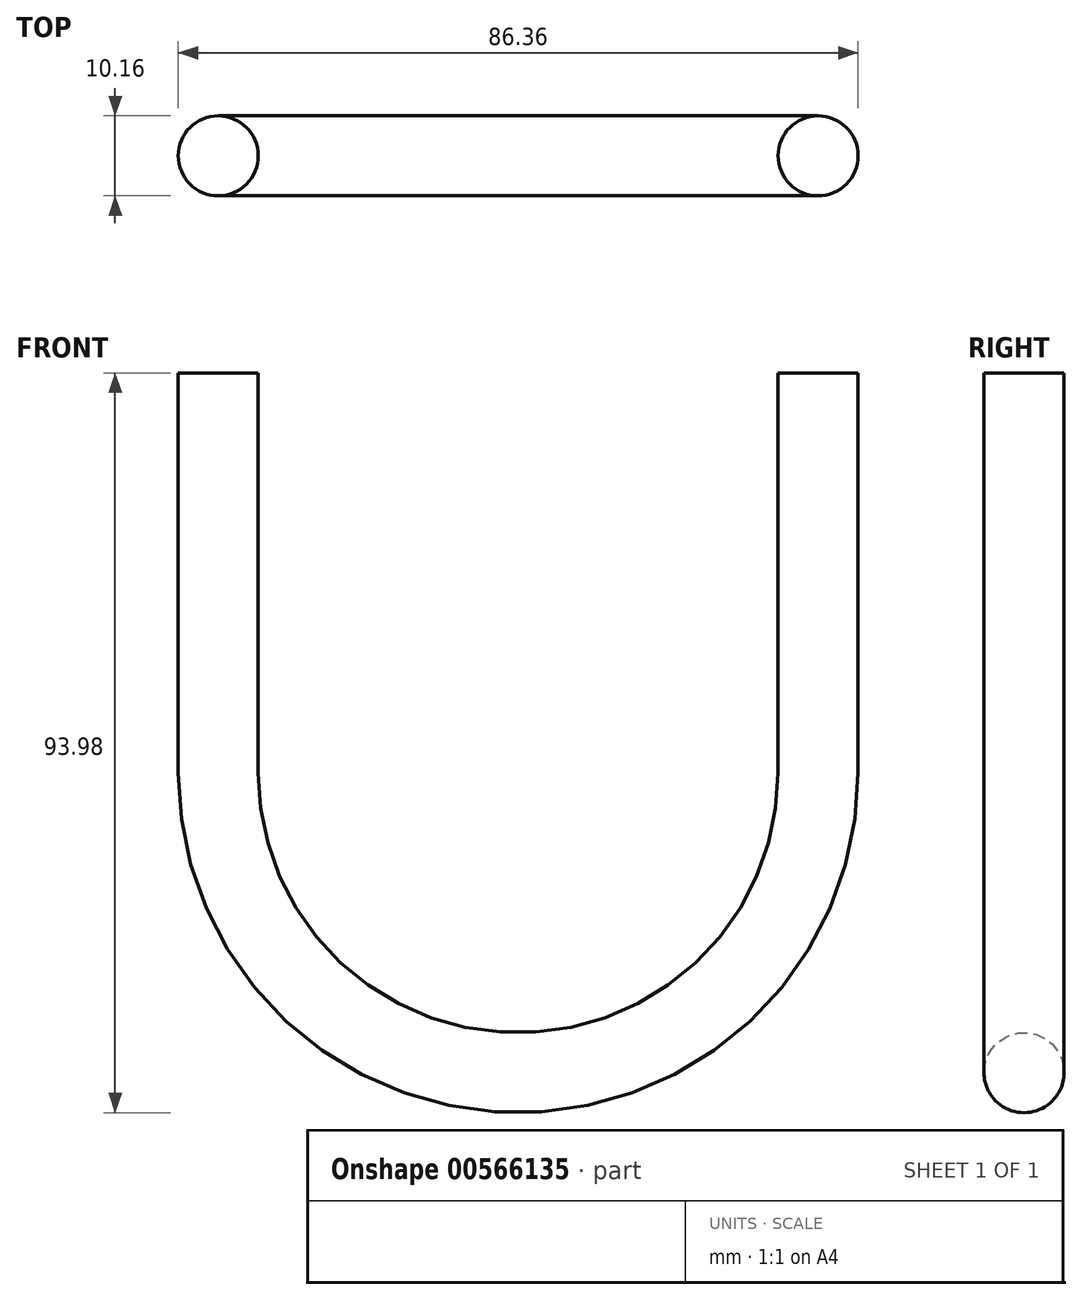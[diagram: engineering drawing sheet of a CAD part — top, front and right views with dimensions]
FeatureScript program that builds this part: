
annotation { "Feature Type Name" : "Feature", "Feature Type Description" : "" }
export const myFeature = defineFeature(function(context is Context, id is Id, definition is map)
    precondition{}
    {
        {
            var Q0;
            Q0=qCreatedBy(makeId("Front.planeOp"),FACE);
            var sketch = newSketch(context, id + "F0", { "sketchPlane" : qUnion([Q0])});
            skLineSegment(sketch, "E0", {"start": v(0, 0) * mm, "end": v(0, -50.8) * mm});
            skArc(sketch, "E1", {"start": v(0, -50.8) * mm, "mid": v(-38.1, -88.9) * mm, "end": v(-76.2, -50.8) * mm});
            skLineSegment(sketch, "E2", {"start": v(-76.2, -50.8) * mm, "end": v(-76.2, 0) * mm});
            skSolve(sketch);
        }
        {
            var Q0;
            Q0=sQuery(id+"F0.wireOp",VERTEX,"E0.start");
            var Q1;
            Q1=sQuery(id+"F0.wireOp",EDGE,"E0");
            var Q2;
            Q2 = qBodyType(qCreatedBy(id + "F2" ,EDGE), BodyType.WIRE);
            cPlane(context, id + "F1", {"entities" : qUnion([Q0, Q1, Q2]), "cplaneType" : CPlaneType.LINE_POINT, "offset" : 25.4 * mm, "width" : 152.4 * mm, "height" : 152.4 * mm});
        }
        {
            var Q0;
            Q0=qCreatedBy(id+"F1.planeOp",FACE);
            var sketch = newSketch(context, id + "F2", { "sketchPlane" : qUnion([Q0])});
            skSolve(sketch);
        }
        {
            var Q0;
            Q0=qCreatedBy(id+"F1.planeOp",FACE);
            var sketch = newSketch(context, id + "F3", { "sketchPlane" : qUnion([Q0])});
            skCircle(sketch, "E3", {"center": v(-76.2, 0) * mm, "radius": 5.08 * mm});
            skSolve(sketch);
        }
        {
            var Q0;
            Q0=makeQuery(id+"F3.imprint","IMPRINT",FACE,{"disambiguationData":[TD([[makeQuery(id+"F3.imprint","IMPRINT",EDGE,{"derivedFrom":sQuery(id+"F3.wireOp",EDGE,"E3")}),1.0]])]});
            var Q1;
            Q1=sQuery(id+"F0.wireOp",EDGE,"E2");
            var Q2;
            Q2=sQuery(id+"F0.wireOp",EDGE,"E1");
            var Q3;
            Q3=sQuery(id+"F0.wireOp",EDGE,"E0");
            sweep(context, id + "F4", {"profiles" : qUnion([Q0]), "path" : qUnion([Q1, Q2, Q3])});
        }
    });
